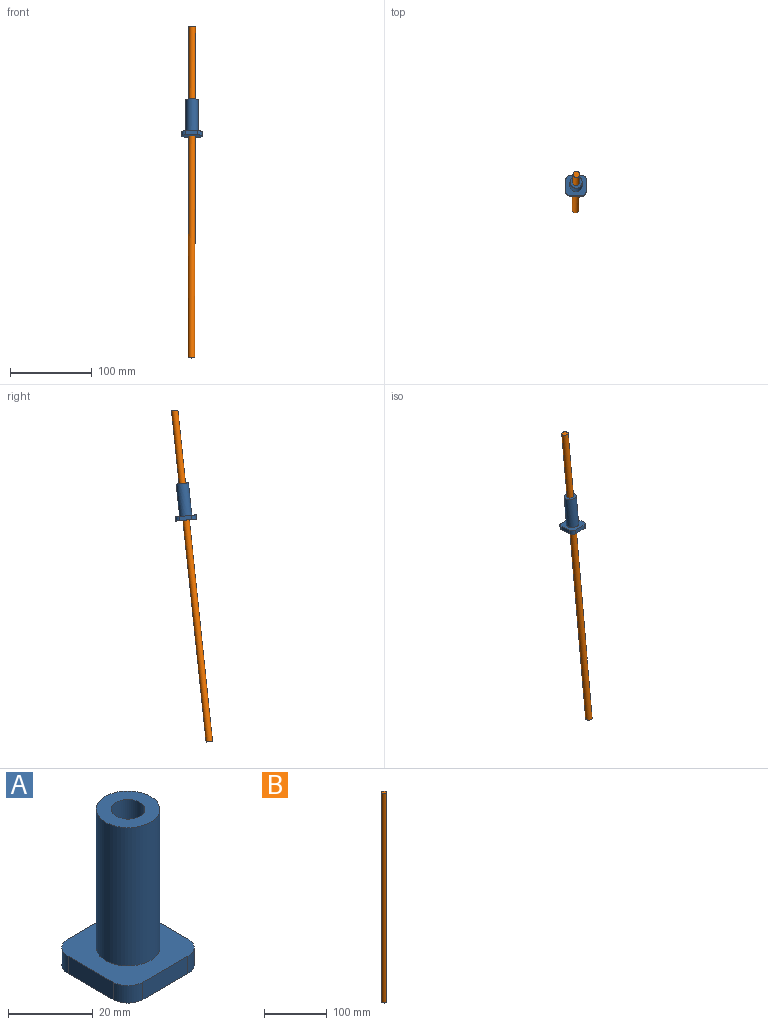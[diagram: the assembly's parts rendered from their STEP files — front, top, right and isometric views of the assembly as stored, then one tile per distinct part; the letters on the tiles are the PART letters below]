
ASSEMBLY  parts=2 mates=1
PART A: 13 faces, bbox 25x25x45 mm
  f0: plane 15x5mm, normal (0,-1,0), area 75mm2, adj f4,f5,f9,f12
  f1: plane 15x5mm, normal (1,0,0), area 75mm2, adj f4,f5,f9,f10
  f2: plane 15x5mm, normal (0,1,0), area 75mm2, adj f4,f5,f10,f11
  f3: plane 15x5mm, normal (-1,0,0), area 75mm2, adj f4,f5,f11,f12
  f4: plane 25x25mm, normal (0,0,1), area 426.8mm2, adj f0,f1,f2,f3,f7,f9,f10,f11
  f5: plane 25x25mm, normal (0,0,-1), area 553.3mm2, adj f0,f1,f2,f3,f6,f9,f10,f11
  f6: cylinder r=4mm len=45mm, axis (0,0,-1), area 1131mm2, adj f5,f8
  f7: cylinder r=7.5mm len=40mm, axis (0,0,-1), area 1885mm2, adj f4,f8
  f8: plane 15x15mm, normal (0,0,1), area 126.4mm2, adj f6,f7
  f9: cylinder r=5mm len=5mm, axis (0,0,-1), area 39.3mm2, adj f0,f1,f4,f5
  f10: cylinder r=5mm len=5mm, axis (0,0,1), area 39.3mm2, adj f1,f2,f4,f5
  f11: cylinder r=5mm len=5mm, axis (0,0,-1), area 39.3mm2, adj f2,f3,f4,f5
  f12: cylinder r=5mm len=5mm, axis (0,0,1), area 39.3mm2, adj f0,f3,f4,f5
PART B: 3 faces, bbox 8x8x408 mm
  f0: cylinder r=4mm len=408mm, axis (0,0,-1), area 10254.2mm2, adj f1,f2
  f1: plane 8x8mm, normal (0,0,1), area 50.3mm2, adj f0
  f2: plane 8x8mm, normal (0,0,-1), area 50.3mm2, adj f0
PLACE A rot(axis=(-0.05,0.05,1),88.8deg) t=(-83.82,-134.8,183.36)mm
PLACE B rot(axis=(-0.05,-0.05,-1),91.5deg) t=(-84.47,-163.15,-88.1)mm
MATE slider B.f0 <-> A.f6  axis (0,-0.1,-0.99) through (-84.47,-163.15,-88.1)mm
